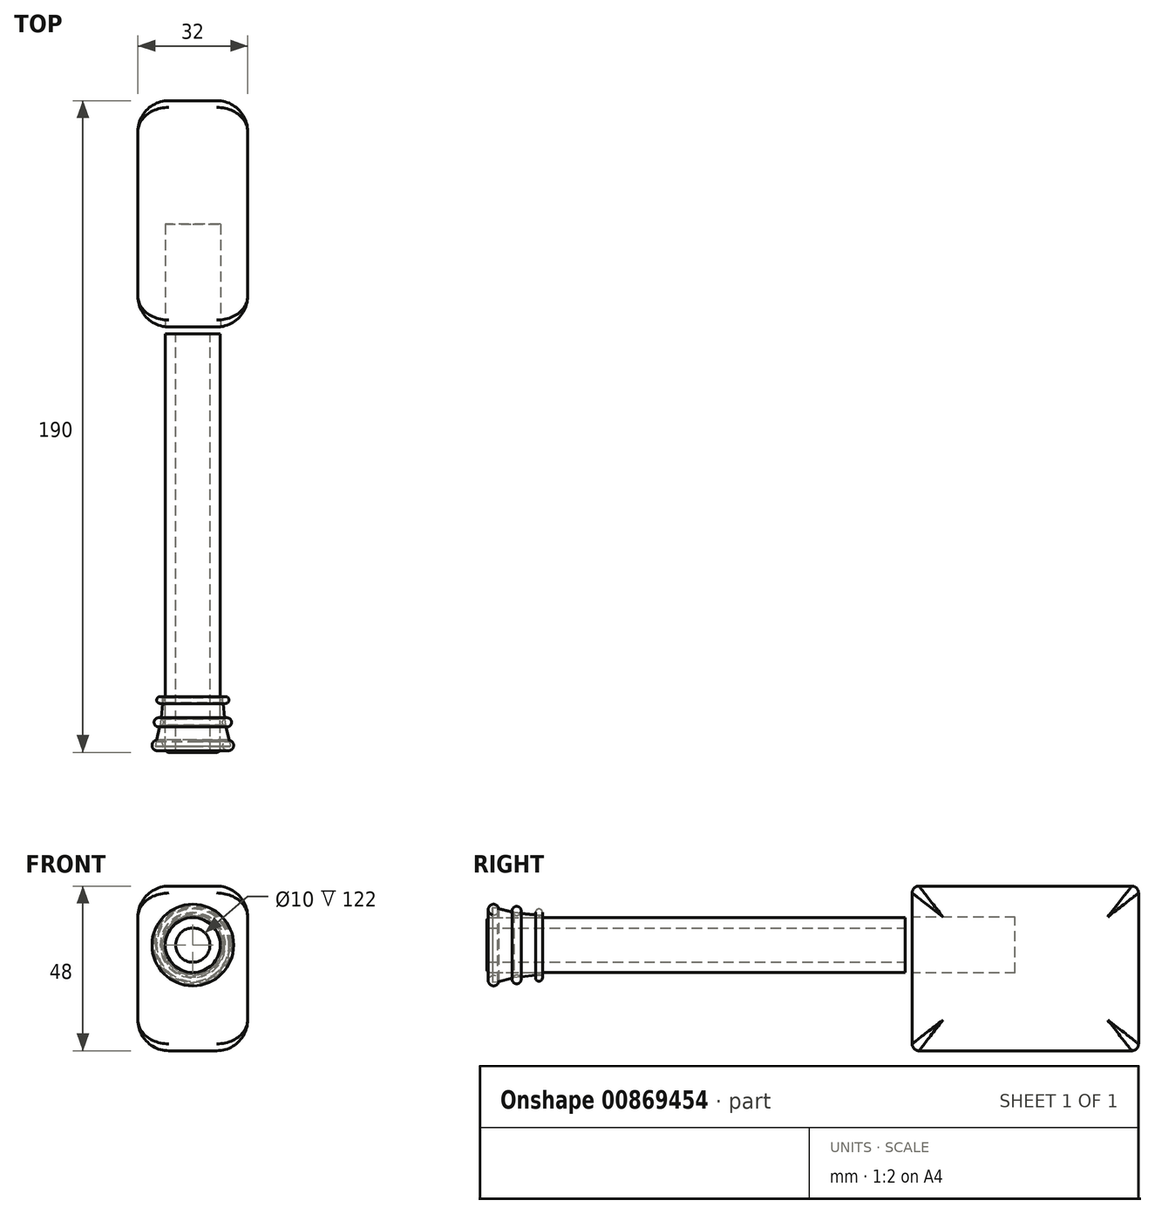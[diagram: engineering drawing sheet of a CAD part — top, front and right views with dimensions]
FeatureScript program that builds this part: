
annotation { "Feature Type Name" : "Feature", "Feature Type Description" : "" }
export const myFeature = defineFeature(function(context is Context, id is Id, definition is map)
    precondition{}
    {
        {
            var Q0;
            Q0=qCreatedBy(makeId("Front.planeOp"),FACE);
            var sketch = newSketch(context, id + "F0", { "sketchPlane" : qUnion([Q0])});
            skCircle(sketch, "E0", {"center": v(0, 0) * mm, "radius": 8 * mm});
            skCircle(sketch, "E1", {"center": v(0, 0) * mm, "radius": 5 * mm});
            skSolve(sketch);
        }
        {
            var Q0;
            Q0=makeQuery(id+"F0.imprint","IMPRINT",FACE,{"disambiguationData":[TD([[makeQuery(id+"F0.imprint","IMPRINT",EDGE,{"derivedFrom":sQuery(id+"F0.wireOp",EDGE,"E0")}),1.0]])]});
            extrude(context, id + "F1", {"entities" : qUnion([Q0]), "depth" : 152 * mm, "offsetDistance" : 25 * mm});
        }
        {
            var Q0;
            Q0=makeQuery(id+"F1.opExtrude","CAP_EDGE",EDGE,{"disambiguationData":[OSD([sQuery(id+"F0.wireOp",EDGE,"E0")])],"isStart":false});
            fillet(context, id + "F2", {"entities" : qUnion([Q0]), "radius" : 1 * mm, "tangentPropagation" : true, "allowEdgeOverflow" : false});
        }
        {
            var Q0;
            Q0=makeQuery(id+"F1.opExtrude","CAP_EDGE",EDGE,{"disambiguationData":[OSD([sQuery(id+"F0.wireOp",EDGE,"E0")])],"isStart":true});
            fillet(context, id + "F3", {"entities" : qUnion([Q0]), "radius" : 1 * mm, "tangentPropagation" : true, "allowEdgeOverflow" : false});
        }
        {
            var Q0;
            Q0=qCreatedBy(makeId("Front.planeOp"),FACE);
            var sketch = newSketch(context, id + "F4", { "sketchPlane" : qUnion([Q0])});
            skLineSegment(sketch, "E2.bottom", {"start": v(16, 17.2) * mm, "end": v(-16, 17.2) * mm});
            skLineSegment(sketch, "E2.top", {"start": v(16, -30.8) * mm, "end": v(-16, -30.8) * mm});
            skLineSegment(sketch, "E2.left", {"start": v(16, 17.2) * mm, "end": v(16, -30.8) * mm});
            skLineSegment(sketch, "E2.right", {"start": v(-16, 17.2) * mm, "end": v(-16, -30.8) * mm});
            skPoint(sketch, "E2.middle", {"position": v(0, -6.8) * mm});
            skSolve(sketch);
        }
        {
            var Q0;
            Q0 = qSketchRegion(id + "F4", true);
            extrude(context, id + "F5", {"entities" : qUnion([Q0]), "depth" : 28 * mm, "offsetDistance" : 25 * mm, "hasSecondDirection" : true, "secondDirectionOppositeDirection" : true, "secondDirectionDepth" : 38 * mm});
        }
        {
            var Q0;
            Q0=qCreatedBy(makeId("Front.planeOp"),FACE);
            var sketch = newSketch(context, id + "F6", { "sketchPlane" : qUnion([Q0])});
            skCircle(sketch, "E3", {"center": v(0, 0) * mm, "radius": 8.1 * mm});
            skSolve(sketch);
        }
        {
            var Q0;
            Q0 = qSketchRegion(id + "F6", true);
            extrude(context, id + "F7", {"entities" : qUnion([Q0]), "operationType" : NewBodyOperationType.REMOVE, "oppositeDirection" : true, "depth" : 2 * mm, "offsetDistance" : 25 * mm, "hasSecondDirection" : true, "secondDirectionOppositeDirection" : false, "secondDirectionDepth" : 30 * mm});
        }
        {
            var Q0;
            Q0=makeQuery(id+"F5.opExtrude","CAP_EDGE",EDGE,{"disambiguationData":[OSD([sQuery(id+"F4.wireOp",EDGE,"E2.right")])],"isStart":false});
            var Q1;
            Q1=makeQuery(id+"F5.opExtrude","SWEPT_EDGE",EDGE,{"disambiguationData":[OSD([sQuery(id+"F4.wireOp",EDGE,"E2.top"),sQuery(id+"F4.wireOp",EDGE,"E2.left")])]});
            var Q2;
            Q2=makeQuery(id+"F5.opExtrude","SWEPT_FACE",FACE,{"disambiguationData":[OSD([sQuery(id+"F4.wireOp",EDGE,"E2.right")])]});
            var Q3;
            Q3=makeQuery(id+"F5.opExtrude","SWEPT_EDGE",EDGE,{"disambiguationData":[OSD([sQuery(id+"F4.wireOp",EDGE,"E2.bottom"),sQuery(id+"F4.wireOp",EDGE,"E2.left")])]});
            var Q4;
            Q4=makeQuery(id+"F5.opExtrude","CAP_EDGE",EDGE,{"disambiguationData":[OSD([sQuery(id+"F4.wireOp",EDGE,"E2.left")])],"isStart":false});
            var Q5;
            Q5=makeQuery(id+"F5.opExtrude","CAP_EDGE",EDGE,{"disambiguationData":[OSD([sQuery(id+"F4.wireOp",EDGE,"E2.left")])],"isStart":true});
            fillet(context, id + "F8", {"entities" : qUnion([Q0, Q1, Q2, Q3, Q4, Q5]), "radius" : 9 * mm, "tangentPropagation" : true, "allowEdgeOverflow" : false});
        }
        {
            var Q0;
            Q0=makeQuery(id+"F5.opExtrude","CAP_EDGE",EDGE,{"disambiguationData":[OSD([sQuery(id+"F4.wireOp",EDGE,"E2.bottom")])],"isStart":false});
            var Q1;
            Q1=makeQuery(id+"F5.opExtrude","CAP_EDGE",EDGE,{"disambiguationData":[OSD([sQuery(id+"F4.wireOp",EDGE,"E2.top")])],"isStart":false});
            var Q2;
            Q2=makeQuery(id+"F5.opExtrude","CAP_EDGE",EDGE,{"disambiguationData":[OSD([sQuery(id+"F4.wireOp",EDGE,"E2.bottom")])],"isStart":true});
            var Q3;
            Q3=makeQuery(id+"F5.opExtrude","CAP_EDGE",EDGE,{"disambiguationData":[OSD([sQuery(id+"F4.wireOp",EDGE,"E2.top")])],"isStart":true});
            fillet(context, id + "F9", {"entities" : qUnion([Q0, Q1, Q2, Q3]), "radius" : 2 * mm, "tangentPropagation" : true, "allowEdgeOverflow" : false});
        }
        {
            var Q0;
            Q0=qCreatedBy(makeId("Right.planeOp"),FACE);
            var sketch = newSketch(context, id + "F10", { "sketchPlane" : qUnion([Q0])});
            skCircle(sketch, "E4", {"center": v(-149.98, 10.34) * mm, "radius": 1.55 * mm});
            skCircle(sketch, "E5", {"center": v(-143.26, 9.97) * mm, "radius": 1.32 * mm});
            skCircle(sketch, "E6", {"center": v(-136.75, 9.52) * mm, "radius": 1.01 * mm});
            skLineSegment(sketch, "E7", {"start": v(0, 0) * mm, "end": v(-95.56, 0) * mm, "construction": true});
            skSolve(sketch);
        }
        {
            var Q0;
            Q0=makeQuery(id+"F10.imprint","IMPRINT",FACE,{"disambiguationData":[TD([[makeQuery(id+"F10.imprint","IMPRINT",EDGE,{"derivedFrom":sQuery(id+"F10.wireOp",EDGE,"E4")}),1.0]])]});
            var Q1;
            Q1=makeQuery(id+"F10.imprint","IMPRINT",FACE,{"disambiguationData":[TD([[makeQuery(id+"F10.imprint","IMPRINT",EDGE,{"derivedFrom":sQuery(id+"F10.wireOp",EDGE,"E5")}),1.0]])]});
            var Q2;
            Q2=makeQuery(id+"F10.imprint","IMPRINT",FACE,{"disambiguationData":[TD([[makeQuery(id+"F10.imprint","IMPRINT",EDGE,{"derivedFrom":sQuery(id+"F10.wireOp",EDGE,"E6")}),1.0]])]});
            var Q3;
            Q3=sQuery(id+"F10.wireOp",EDGE,"E7");
            revolve(context, id + "F11", {"surfaceOperationType" : NewSurfaceOperationType.NEW, "entities" : qUnion([Q0, Q1, Q2]), "axis" : qUnion([Q3]), "revolveType" : RevolveType.FULL});
        }
        {
            var Q0;
            Q0=qCreatedBy(makeId("Right.planeOp"),FACE);
            var sketch = newSketch(context, id + "F12", { "sketchPlane" : qUnion([Q0])});
            skLineSegment(sketch, "E8", {"start": v(-150.33, 10.9) * mm, "end": v(-148.9, 10.73) * mm});
            skLineSegment(sketch, "E9", {"start": v(-148.9, 10.73) * mm, "end": v(-144.11, 9.5) * mm});
            skLineSegment(sketch, "E10", {"start": v(-144.11, 9.5) * mm, "end": v(-142.21, 9.25) * mm});
            skLineSegment(sketch, "E11", {"start": v(-142.21, 9.25) * mm, "end": v(-137.63, 8.79) * mm});
            skLineSegment(sketch, "E12", {"start": v(-137.63, 8.79) * mm, "end": v(-136, 8.79) * mm});
            skLineSegment(sketch, "E13", {"start": v(-136, 8.79) * mm, "end": v(-136, 8) * mm});
            skLineSegment(sketch, "E14", {"start": v(-136, 8) * mm, "end": v(-150.3, 8) * mm});
            skLineSegment(sketch, "E15", {"start": v(-150.3, 8) * mm, "end": v(-150.33, 10.9) * mm});
            skSolve(sketch);
        }
        {
            var Q0;
            Q0 = qSketchRegion(id + "F12", true);
            var Q1;
            Q1=makeQuery(id+"F1.opExtrude","SWEPT_FACE",FACE,{"disambiguationData":[OSD([sQuery(id+"F0.wireOp",EDGE,"E1")])]});
            revolve(context, id + "F13", {"surfaceOperationType" : NewSurfaceOperationType.NEW, "entities" : qUnion([Q0]), "axis" : qUnion([Q1]), "revolveType" : RevolveType.FULL});
        }
    });
